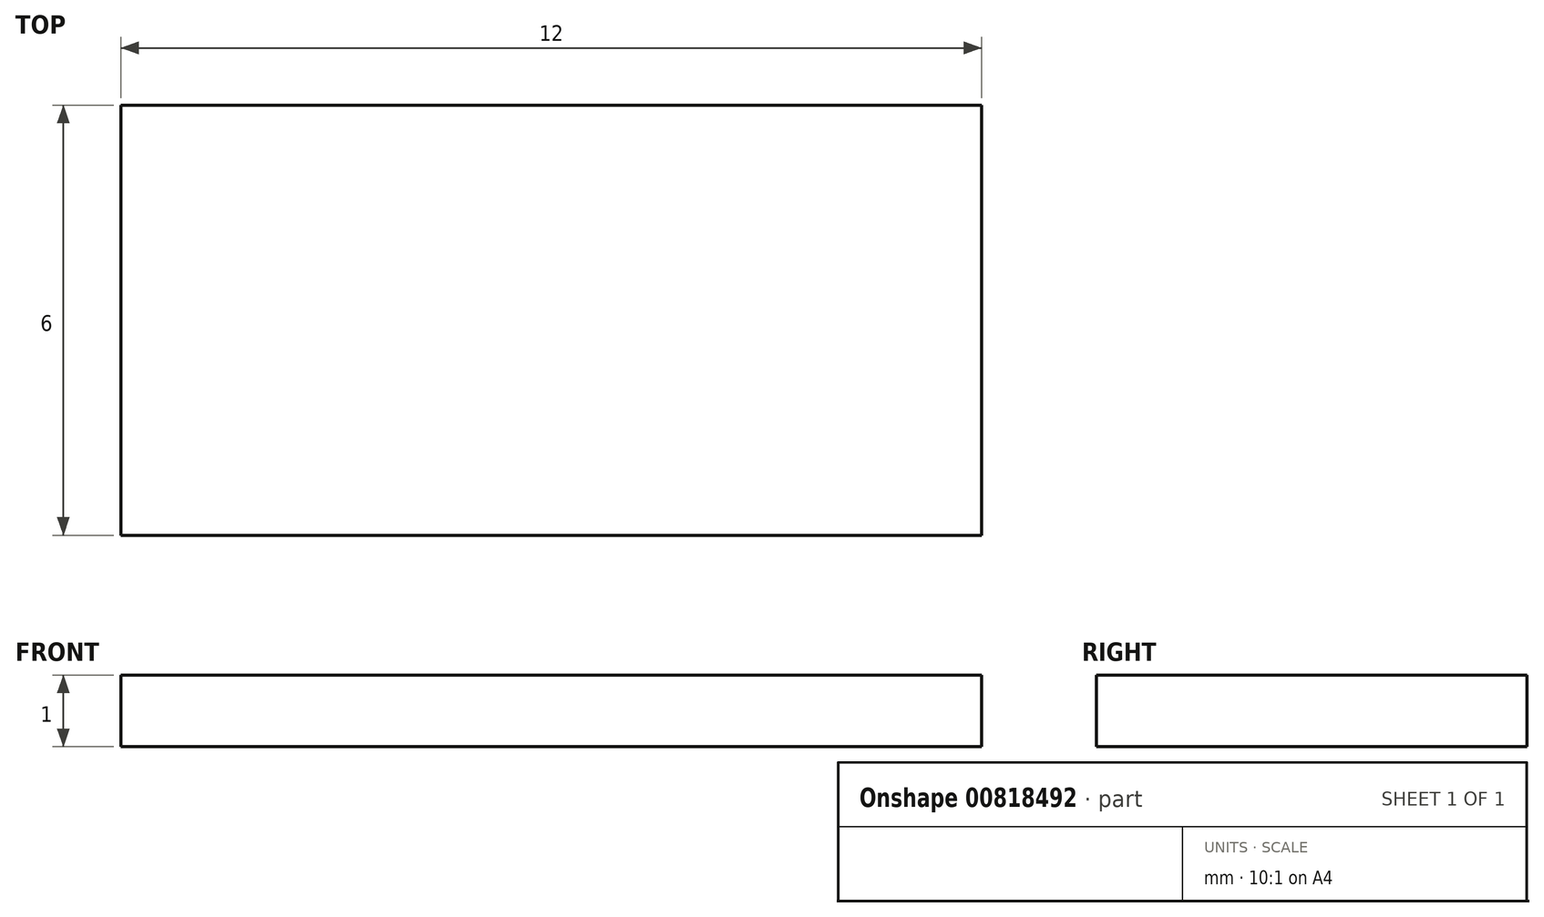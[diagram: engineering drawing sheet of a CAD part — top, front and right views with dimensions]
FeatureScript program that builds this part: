
annotation { "Feature Type Name" : "Feature", "Feature Type Description" : "" }
export const myFeature = defineFeature(function(context is Context, id is Id, definition is map)
    precondition{}
    {
        {
            var Q0;
            Q0=qCreatedBy(makeId("Top.planeOp"),FACE);
            var sketch = newSketch(context, id + "F0", { "sketchPlane" : qUnion([Q0])});
            skLineSegment(sketch, "E0.bottom", {"start": v(6, -3) * mm, "end": v(-6, -3) * mm});
            skLineSegment(sketch, "E0.top", {"start": v(6, 3) * mm, "end": v(-6, 3) * mm});
            skLineSegment(sketch, "E0.left", {"start": v(6, -3) * mm, "end": v(6, 3) * mm});
            skLineSegment(sketch, "E0.right", {"start": v(-6, -3) * mm, "end": v(-6, 3) * mm});
            skPoint(sketch, "E0.middle", {"position": v(0, 0) * mm});
            skSolve(sketch);
        }
        {
            var Q0;
            Q0 = qSketchRegion(id + "F0", true);
            extrude(context, id + "F1", {"entities" : qUnion([Q0]), "depth" : 1 * mm, "offsetDistance" : 25 * mm});
        }
    });
